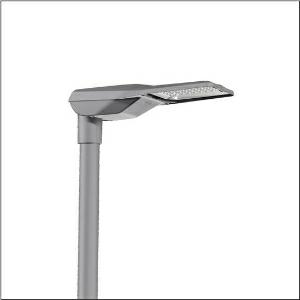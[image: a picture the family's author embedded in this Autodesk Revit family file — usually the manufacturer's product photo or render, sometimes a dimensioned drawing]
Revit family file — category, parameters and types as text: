
# Revit family: streetlight_sl_21_mini___st1_0a_5xe6d23a08hb_20ef
name_source: partatom
category: Lighting Fixtures
units: mm (PartAtom-declared; Revit-internal decimal feet)

## family parameters
Cut with Voids When Loaded = No
Host = Face
Light Source = No
Part Type = Normal
Room Calculation Point = No
Round Connector Dimension = Use Diameter
Shared = No

## types (1)
- --- (1 x LED, 7490 lm, 66 W, 2200K)
    Apparent Load = 66 VA
    CIE Flux Codes = 37 72 97 100 100
    Color Rendering = 70
    Color Temperature = 2200K
    Default Elevation = 1800 mm
    Description = Streetlight SL 21 mini, mast luminaire, primary light control with lens, of PMMA, primary optical cover: cover, of toughened safety glass, transparent, light distribution: ST1.0a, light emission: direct distribution, primary light characteristic: asymmetric, installation type: post-top, side-entry, LED, 3G 1.5mm², High Power LED, rated luminous flux: 7.490lm, luminous efficacy: 114lm/W, light colour: 722, colour temperature: 2200K, control gear: Easy, control: overheat protection, constant luminous flux control, time-dependent luminous flux control, flexible luminous flux parameterisation, mains connection: 230..240V, AC, 50/60Hz, connection cable pre-assembled, cable length: 8,5m, wiring characteristics: H07RN-F, start of lifetime: 66W, end of service life: 69W, reduction: 30W, luminaire housing, of diecast aluminium, powder-coated, Siteco® metallic grey (DB 702S), corrosivity category C5 mid according to DIN EN ISO 12944, please order mast flange separately, inclination adjustable: 0°, 5°, 10°, 15°, sealing non-destructively replaceable, multi-level sealing system, length: 628mm, width: 235mm, height: 110mm, mast flange for spigot size: 42mm (side-entry): 5XC10008XM4, 60/48mm (side-entry/post-top): 5XC10108XM2, 76/60mm (side-entry/post-top): 5XC10108XM1, mounting height: 4..8m, protection rating (complete): IP66, insulation class (complete): insulation class II (safety insulation), certification: CE, ENEC, ENEC+, VDE, impact resistance: IK10, permissible operating ambient temperature for outdoor applications: -40..+50°C, standard-compliant lighting for roads and squares, packaging unit: 1 piece

Light Distribution: ST1.0a
    Height = 110 mm
    Lamp = 1 x LED
    Lamp Light Flux = 7490 lm
    Lamp Power = 66 W
    Lamp count = 1
    Length = 625 mm
    Luminous efficacy = 113 lm/W
    Manufacturer = Siteco
    ModVariant = No
    Model = 5XE6D23A08HB
    Number of Poles = 1
    OnlyDefault = Yes
    Power Factor = 1
    Product Name = Streetlight SL 21 mini | ST1.0a
    Product group = mast luminaire | pylon top
    ProductGroupID = 6100
    Protection Class = Protection class II
    Protection Degree = IP 66
    RLX_Detail_Level = 1
    RLX_Emergency_Light_Flux = 0 lm
    RLX_Emergency_Type = 0
    RLX_Emergency_Type_DB = No
    RlxData = <blob elided: 26061 chars, md5=fd7498ce>
    Socket = socket
    Standby Power = 0 W
    System Light Flux = 7490 lm
    System Power = 66 W
    Type Comments = factory setting: luminous flux: 100 % | Output Level: 100 % | 670 mA
    Type Image = l_1003519.jpg
    URL = http://relux.com
    VarID = @adj_209589
    Voltage = 0 V
    Weight = 0.00 kg
    Width = 234 mm

## geometry (parser evidence)
native form markers: Blend x4, Sweep x12
no freeform markers — native parametric forms only
